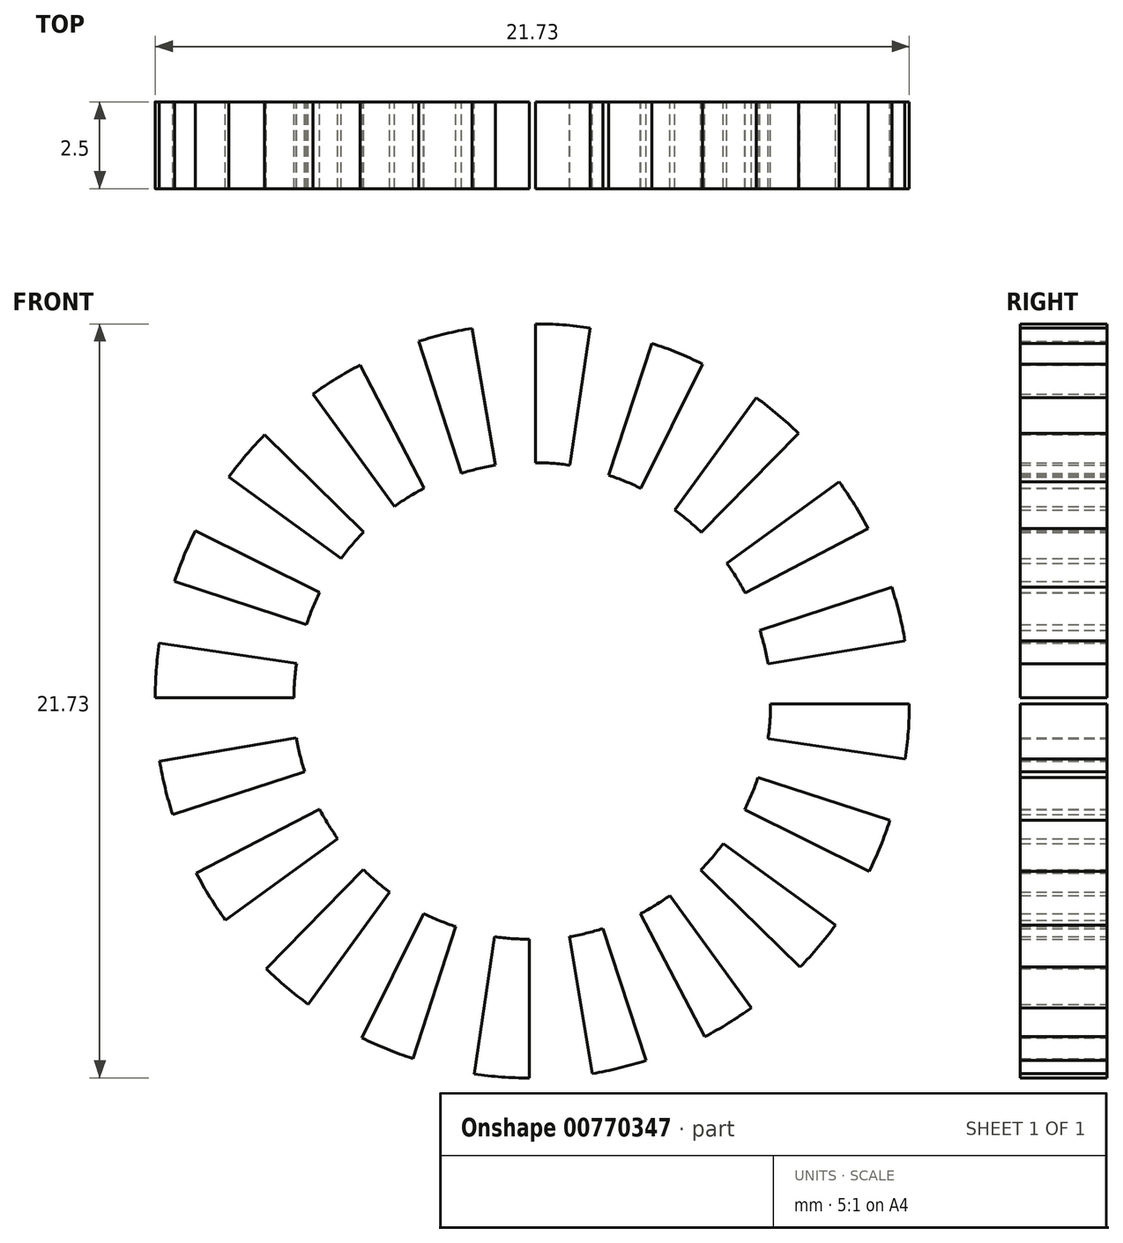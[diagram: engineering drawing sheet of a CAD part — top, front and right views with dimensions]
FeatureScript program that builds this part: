
annotation { "Feature Type Name" : "Feature", "Feature Type Description" : "" }
export const myFeature = defineFeature(function(context is Context, id is Id, definition is map)
    precondition{}
    {
        {
            var Q0;
            Q0=qCreatedBy(makeId("Front.planeOp"),FACE);
            var sketch = newSketch(context, id + "F0", { "sketchPlane" : qUnion([Q0])});
            skCircle(sketch, "E0", {"center": v(0, 0) * mm, "radius": 11.8 * mm});
            skSolve(sketch);
        }
        {
            var Q0;
            Q0=makeQuery(id+"F0.imprint","IMPRINT",FACE,{"disambiguationData":[TD([[makeQuery(id+"F0.imprint","IMPRINT",EDGE,{"derivedFrom":sQuery(id+"F0.wireOp",EDGE,"E0")}),1.0]])]});
            extrude(context, id + "F1", {"entities" : qUnion([Q0]), "endBound" : BoundingType.SYMMETRIC, "depth" : 2.5 * mm, "offsetDistance" : 25 * mm});
        }
        {
            var Q0;
            Q0=makeQuery(id+"F1.opExtrude","CAP_FACE",FACE,{"disambiguationData":[OSD([sQuery(id+"F0.wireOp",EDGE,"E0")])],"isStart":true});
            var sketch = newSketch(context, id + "F2", { "sketchPlane" : qUnion([Q0])});
            skArc(sketch, "E1", {"start": v(-1.58, 10.68) * mm, "mid": v(-0.8, 10.77) * mm, "end": v(0, 10.8) * mm});
            skArc(sketch, "E2", {"start": v(-1, 6.73) * mm, "mid": v(-0.5, 6.78) * mm, "end": v(0, 6.8) * mm});
            skLineSegment(sketch, "E3", {"start": v(-1, 6.73) * mm, "end": v(-1.58, 10.68) * mm});
            skLineSegment(sketch, "E4", {"start": v(0, 6.8) * mm, "end": v(0, 10.8) * mm});
            skArc(sketch, "E5.1.0", {"start": v(-4.82, 9.64) * mm, "mid": v(-4.1, 9.97) * mm, "end": v(-3.35, 10.24) * mm});
            skArc(sketch, "E5.1.1", {"start": v(-3.04, 6.06) * mm, "mid": v(-2.59, 6.26) * mm, "end": v(-2.12, 6.44) * mm});
            skLineSegment(sketch, "E5.1.2", {"start": v(-2.12, 6.44) * mm, "end": v(-3.35, 10.24) * mm});
            skLineSegment(sketch, "E5.1.3", {"start": v(-3.04, 6.06) * mm, "end": v(-4.82, 9.64) * mm});
            skArc(sketch, "E5.2.0", {"start": v(-7.58, 7.65) * mm, "mid": v(-7, 8.18) * mm, "end": v(-6.37, 8.67) * mm});
            skArc(sketch, "E5.2.1", {"start": v(-4.78, 4.8) * mm, "mid": v(-4.41, 5.13) * mm, "end": v(-4.02, 5.44) * mm});
            skLineSegment(sketch, "E5.2.2", {"start": v(-4.02, 5.44) * mm, "end": v(-6.37, 8.67) * mm});
            skLineSegment(sketch, "E5.2.3", {"start": v(-4.78, 4.8) * mm, "end": v(-7.58, 7.65) * mm});
            skArc(sketch, "E5.3.0", {"start": v(-9.6, 4.9) * mm, "mid": v(-9.2, 5.6) * mm, "end": v(-8.76, 6.25) * mm});
            skArc(sketch, "E5.3.1", {"start": v(-6.05, 3.05) * mm, "mid": v(-5.8, 3.48) * mm, "end": v(-5.52, 3.9) * mm});
            skLineSegment(sketch, "E5.3.2", {"start": v(-5.52, 3.9) * mm, "end": v(-8.76, 6.25) * mm});
            skLineSegment(sketch, "E5.3.3", {"start": v(-6.05, 3.05) * mm, "end": v(-9.6, 4.9) * mm});
            skArc(sketch, "E5.4.0", {"start": v(-10.65, 1.67) * mm, "mid": v(-10.5, 2.44) * mm, "end": v(-10.28, 3.2) * mm});
            skArc(sketch, "E5.4.1", {"start": v(-6.7, 1) * mm, "mid": v(-6.6, 1.5) * mm, "end": v(-6.47, 1.97) * mm});
            skLineSegment(sketch, "E5.4.2", {"start": v(-6.47, 1.97) * mm, "end": v(-10.28, 3.2) * mm});
            skLineSegment(sketch, "E5.4.3", {"start": v(-6.7, 1) * mm, "end": v(-10.65, 1.67) * mm});
            skArc(sketch, "E5.5.0", {"start": v(-10.66, -1.74) * mm, "mid": v(-10.75, -0.95) * mm, "end": v(-10.78, -0.15) * mm});
            skArc(sketch, "E5.5.1", {"start": v(-6.7, -1.15) * mm, "mid": v(-6.76, -0.65) * mm, "end": v(-6.78, -0.15) * mm});
            skLineSegment(sketch, "E5.5.2", {"start": v(-6.78, -0.15) * mm, "end": v(-10.78, -0.15) * mm});
            skLineSegment(sketch, "E5.5.3", {"start": v(-6.7, -1.15) * mm, "end": v(-10.66, -1.74) * mm});
            skArc(sketch, "E5.6.0", {"start": v(-9.62, -4.98) * mm, "mid": v(-9.95, -4.25) * mm, "end": v(-10.22, -3.5) * mm});
            skArc(sketch, "E5.6.1", {"start": v(-6.04, -3.2) * mm, "mid": v(-6.24, -2.74) * mm, "end": v(-6.42, -2.27) * mm});
            skLineSegment(sketch, "E5.6.2", {"start": v(-6.42, -2.27) * mm, "end": v(-10.22, -3.5) * mm});
            skLineSegment(sketch, "E5.6.3", {"start": v(-6.04, -3.2) * mm, "end": v(-9.62, -4.98) * mm});
            skArc(sketch, "E5.7.0", {"start": v(-7.63, -7.74) * mm, "mid": v(-8.16, -7.15) * mm, "end": v(-8.65, -6.53) * mm});
            skArc(sketch, "E5.7.1", {"start": v(-4.77, -4.94) * mm, "mid": v(-5.1, -4.57) * mm, "end": v(-5.42, -4.17) * mm});
            skLineSegment(sketch, "E5.7.2", {"start": v(-5.42, -4.17) * mm, "end": v(-8.65, -6.53) * mm});
            skLineSegment(sketch, "E5.7.3", {"start": v(-4.77, -4.94) * mm, "end": v(-7.63, -7.74) * mm});
            skArc(sketch, "E5.8.0", {"start": v(-4.88, -9.75) * mm, "mid": v(-5.57, -9.35) * mm, "end": v(-6.23, -8.91) * mm});
            skArc(sketch, "E5.8.1", {"start": v(-3.03, -6.2) * mm, "mid": v(-3.46, -5.95) * mm, "end": v(-3.88, -5.67) * mm});
            skLineSegment(sketch, "E5.8.2", {"start": v(-3.88, -5.67) * mm, "end": v(-6.23, -8.91) * mm});
            skLineSegment(sketch, "E5.8.3", {"start": v(-3.03, -6.2) * mm, "end": v(-4.88, -9.75) * mm});
            skArc(sketch, "E5.9.0", {"start": v(-1.65, -10.8) * mm, "mid": v(-2.42, -10.65) * mm, "end": v(-3.19, -10.43) * mm});
            skArc(sketch, "E5.9.1", {"start": v(-0.98, -6.86) * mm, "mid": v(-1.47, -6.76) * mm, "end": v(-1.95, -6.63) * mm});
            skLineSegment(sketch, "E5.9.2", {"start": v(-1.95, -6.63) * mm, "end": v(-3.19, -10.43) * mm});
            skLineSegment(sketch, "E5.9.3", {"start": v(-0.98, -6.86) * mm, "end": v(-1.65, -10.8) * mm});
            skArc(sketch, "E5.10.0", {"start": v(1.76, -10.82) * mm, "mid": v(0.97, -10.9) * mm, "end": v(0.17, -10.93) * mm});
            skArc(sketch, "E5.10.1", {"start": v(1.17, -6.86) * mm, "mid": v(0.67, -6.92) * mm, "end": v(0.17, -6.93) * mm});
            skLineSegment(sketch, "E5.10.2", {"start": v(0.17, -6.93) * mm, "end": v(0.17, -10.93) * mm});
            skLineSegment(sketch, "E5.10.3", {"start": v(1.17, -6.86) * mm, "end": v(1.76, -10.82) * mm});
            skArc(sketch, "E5.11.0", {"start": v(5, -9.78) * mm, "mid": v(4.27, -10.1) * mm, "end": v(3.53, -10.38) * mm});
            skArc(sketch, "E5.11.1", {"start": v(3.22, -6.2) * mm, "mid": v(2.76, -6.4) * mm, "end": v(2.3, -6.57) * mm});
            skLineSegment(sketch, "E5.11.2", {"start": v(2.3, -6.57) * mm, "end": v(3.53, -10.38) * mm});
            skLineSegment(sketch, "E5.11.3", {"start": v(3.22, -6.2) * mm, "end": v(5, -9.78) * mm});
            skArc(sketch, "E5.12.0", {"start": v(7.76, -7.78) * mm, "mid": v(7.17, -8.32) * mm, "end": v(6.55, -8.8) * mm});
            skArc(sketch, "E5.12.1", {"start": v(4.96, -4.93) * mm, "mid": v(4.59, -5.26) * mm, "end": v(4.2, -5.57) * mm});
            skLineSegment(sketch, "E5.12.2", {"start": v(4.2, -5.57) * mm, "end": v(6.55, -8.8) * mm});
            skLineSegment(sketch, "E5.12.3", {"start": v(4.96, -4.93) * mm, "end": v(7.76, -7.78) * mm});
            skArc(sketch, "E5.13.0", {"start": v(9.77, -5.03) * mm, "mid": v(9.37, -5.72) * mm, "end": v(8.93, -6.38) * mm});
            skArc(sketch, "E5.13.1", {"start": v(6.22, -3.18) * mm, "mid": v(5.97, -3.62) * mm, "end": v(5.7, -4.03) * mm});
            skLineSegment(sketch, "E5.13.2", {"start": v(5.7, -4.03) * mm, "end": v(8.93, -6.38) * mm});
            skLineSegment(sketch, "E5.13.3", {"start": v(6.22, -3.18) * mm, "end": v(9.77, -5.03) * mm});
            skArc(sketch, "E5.14.0", {"start": v(10.83, -1.8) * mm, "mid": v(10.67, -2.58) * mm, "end": v(10.45, -3.34) * mm});
            skArc(sketch, "E5.14.1", {"start": v(6.88, -1.14) * mm, "mid": v(6.78, -1.63) * mm, "end": v(6.65, -2.1) * mm});
            skLineSegment(sketch, "E5.14.2", {"start": v(6.65, -2.1) * mm, "end": v(10.45, -3.34) * mm});
            skLineSegment(sketch, "E5.14.3", {"start": v(6.88, -1.14) * mm, "end": v(10.83, -1.8) * mm});
            skArc(sketch, "E5.15.0", {"start": v(10.84, 1.6) * mm, "mid": v(10.93, 0.81) * mm, "end": v(10.95, 0.02) * mm});
            skArc(sketch, "E5.15.1", {"start": v(6.88, 1.02) * mm, "mid": v(6.94, 0.52) * mm, "end": v(6.95, 0.02) * mm});
            skLineSegment(sketch, "E5.15.2", {"start": v(6.95, 0.02) * mm, "end": v(10.95, 0.02) * mm});
            skLineSegment(sketch, "E5.15.3", {"start": v(6.88, 1.02) * mm, "end": v(10.84, 1.6) * mm});
            skArc(sketch, "E5.16.0", {"start": v(9.8, 4.84) * mm, "mid": v(10.12, 4.12) * mm, "end": v(10.4, 3.37) * mm});
            skArc(sketch, "E5.16.1", {"start": v(6.21, 3.06) * mm, "mid": v(6.42, 2.6) * mm, "end": v(6.6, 2.14) * mm});
            skLineSegment(sketch, "E5.16.2", {"start": v(6.6, 2.14) * mm, "end": v(10.4, 3.37) * mm});
            skLineSegment(sketch, "E5.16.3", {"start": v(6.21, 3.06) * mm, "end": v(9.8, 4.84) * mm});
            skArc(sketch, "E5.17.0", {"start": v(7.8, 7.6) * mm, "mid": v(8.34, 7.02) * mm, "end": v(8.83, 6.4) * mm});
            skArc(sketch, "E5.17.1", {"start": v(4.95, 4.8) * mm, "mid": v(5.28, 4.43) * mm, "end": v(5.6, 4.04) * mm});
            skLineSegment(sketch, "E5.17.2", {"start": v(5.6, 4.04) * mm, "end": v(8.83, 6.4) * mm});
            skLineSegment(sketch, "E5.17.3", {"start": v(4.95, 4.8) * mm, "end": v(7.8, 7.6) * mm});
            skArc(sketch, "E5.18.0", {"start": v(5.05, 9.61) * mm, "mid": v(5.74, 9.22) * mm, "end": v(6.4, 8.78) * mm});
            skArc(sketch, "E5.18.1", {"start": v(3.2, 6.07) * mm, "mid": v(3.64, 5.82) * mm, "end": v(4.05, 5.54) * mm});
            skLineSegment(sketch, "E5.18.2", {"start": v(4.05, 5.54) * mm, "end": v(6.4, 8.78) * mm});
            skLineSegment(sketch, "E5.18.3", {"start": v(3.2, 6.07) * mm, "end": v(5.05, 9.61) * mm});
            skArc(sketch, "E5.19.0", {"start": v(1.82, 10.67) * mm, "mid": v(2.6, 10.51) * mm, "end": v(3.36, 10.3) * mm});
            skArc(sketch, "E5.19.1", {"start": v(1.16, 6.73) * mm, "mid": v(1.65, 6.63) * mm, "end": v(2.13, 6.5) * mm});
            skLineSegment(sketch, "E5.19.2", {"start": v(2.13, 6.5) * mm, "end": v(3.36, 10.3) * mm});
            skLineSegment(sketch, "E5.19.3", {"start": v(1.16, 6.73) * mm, "end": v(1.82, 10.67) * mm});
            skPoint(sketch, "E5.center", {"position": v(0.09, -0.07) * mm});
            skSolve(sketch);
        }
        {
            var Q0;
            Q0=makeQuery(id+"F2.imprint","IMPRINT",FACE,{"disambiguationData":[TD([[makeQuery(id+"F2.imprint","IMPRINT",EDGE,{"derivedFrom":sQuery(id+"F2.wireOp",EDGE,"E1")}),-1.0]])]});
            var Q1;
            Q1=makeQuery(id+"F2.imprint","IMPRINT",FACE,{"disambiguationData":[TD([[makeQuery(id+"F2.imprint","IMPRINT",EDGE,{"derivedFrom":sQuery(id+"F2.wireOp",EDGE,"E5.2.0")}),-1.0]])]});
            var Q2;
            Q2=makeQuery(id+"F2.imprint","IMPRINT",FACE,{"disambiguationData":[TD([[makeQuery(id+"F2.imprint","IMPRINT",EDGE,{"derivedFrom":sQuery(id+"F2.wireOp",EDGE,"E5.3.0")}),-1.0]])]});
            var Q3;
            Q3=makeQuery(id+"F2.imprint","IMPRINT",FACE,{"disambiguationData":[TD([[makeQuery(id+"F2.imprint","IMPRINT",EDGE,{"derivedFrom":sQuery(id+"F2.wireOp",EDGE,"E5.4.0")}),-1.0]])]});
            var Q4;
            Q4=makeQuery(id+"F2.imprint","IMPRINT",FACE,{"disambiguationData":[TD([[makeQuery(id+"F2.imprint","IMPRINT",EDGE,{"derivedFrom":sQuery(id+"F2.wireOp",EDGE,"E5.5.0")}),-1.0]])]});
            var Q5;
            Q5=makeQuery(id+"F2.imprint","IMPRINT",FACE,{"disambiguationData":[TD([[makeQuery(id+"F2.imprint","IMPRINT",EDGE,{"derivedFrom":sQuery(id+"F2.wireOp",EDGE,"E5.6.0")}),-1.0]])]});
            var Q6;
            Q6=makeQuery(id+"F2.imprint","IMPRINT",FACE,{"disambiguationData":[TD([[makeQuery(id+"F2.imprint","IMPRINT",EDGE,{"derivedFrom":sQuery(id+"F2.wireOp",EDGE,"E5.7.0")}),-1.0]])]});
            var Q7;
            Q7=makeQuery(id+"F2.imprint","IMPRINT",FACE,{"disambiguationData":[TD([[makeQuery(id+"F2.imprint","IMPRINT",EDGE,{"derivedFrom":sQuery(id+"F2.wireOp",EDGE,"E5.8.0")}),-1.0]])]});
            var Q8;
            Q8=makeQuery(id+"F2.imprint","IMPRINT",FACE,{"disambiguationData":[TD([[makeQuery(id+"F2.imprint","IMPRINT",EDGE,{"derivedFrom":sQuery(id+"F2.wireOp",EDGE,"E5.9.0")}),-1.0]])]});
            var Q9;
            Q9=makeQuery(id+"F2.imprint","IMPRINT",FACE,{"disambiguationData":[TD([[makeQuery(id+"F2.imprint","IMPRINT",EDGE,{"derivedFrom":sQuery(id+"F2.wireOp",EDGE,"E5.10.0")}),-1.0]])]});
            var Q10;
            Q10=makeQuery(id+"F2.imprint","IMPRINT",FACE,{"disambiguationData":[TD([[makeQuery(id+"F2.imprint","IMPRINT",EDGE,{"derivedFrom":sQuery(id+"F2.wireOp",EDGE,"E5.11.0")}),-1.0]])]});
            var Q11;
            Q11=makeQuery(id+"F2.imprint","IMPRINT",FACE,{"disambiguationData":[TD([[makeQuery(id+"F2.imprint","IMPRINT",EDGE,{"derivedFrom":sQuery(id+"F2.wireOp",EDGE,"E5.12.0")}),-1.0]])]});
            var Q12;
            Q12=makeQuery(id+"F2.imprint","IMPRINT",FACE,{"disambiguationData":[TD([[makeQuery(id+"F2.imprint","IMPRINT",EDGE,{"derivedFrom":sQuery(id+"F2.wireOp",EDGE,"E5.13.0")}),-1.0]])]});
            var Q13;
            Q13=makeQuery(id+"F2.imprint","IMPRINT",FACE,{"disambiguationData":[TD([[makeQuery(id+"F2.imprint","IMPRINT",EDGE,{"derivedFrom":sQuery(id+"F2.wireOp",EDGE,"E5.14.0")}),-1.0]])]});
            var Q14;
            Q14=makeQuery(id+"F2.imprint","IMPRINT",FACE,{"disambiguationData":[TD([[makeQuery(id+"F2.imprint","IMPRINT",EDGE,{"derivedFrom":sQuery(id+"F2.wireOp",EDGE,"E5.15.0")}),-1.0]])]});
            var Q15;
            Q15=makeQuery(id+"F2.imprint","IMPRINT",FACE,{"disambiguationData":[TD([[makeQuery(id+"F2.imprint","IMPRINT",EDGE,{"derivedFrom":sQuery(id+"F2.wireOp",EDGE,"E5.16.0")}),-1.0]])]});
            var Q16;
            Q16=makeQuery(id+"F2.imprint","IMPRINT",FACE,{"disambiguationData":[TD([[makeQuery(id+"F2.imprint","IMPRINT",EDGE,{"derivedFrom":sQuery(id+"F2.wireOp",EDGE,"E5.17.0")}),-1.0]])]});
            var Q17;
            Q17=makeQuery(id+"F2.imprint","IMPRINT",FACE,{"disambiguationData":[TD([[makeQuery(id+"F2.imprint","IMPRINT",EDGE,{"derivedFrom":sQuery(id+"F2.wireOp",EDGE,"E5.18.0")}),-1.0]])]});
            var Q18;
            Q18=makeQuery(id+"F2.imprint","IMPRINT",FACE,{"disambiguationData":[TD([[makeQuery(id+"F2.imprint","IMPRINT",EDGE,{"derivedFrom":sQuery(id+"F2.wireOp",EDGE,"E5.19.0")}),-1.0]])]});
            var Q19;
            Q19=makeQuery(id+"F2.imprint","IMPRINT",FACE,{"disambiguationData":[TD([[makeQuery(id+"F2.imprint","IMPRINT",EDGE,{"derivedFrom":sQuery(id+"F2.wireOp",EDGE,"E5.1.0")}),-1.0]])]});
            extrude(context, id + "F3", {"entities" : qUnion([Q0, Q1, Q2, Q3, Q4, Q5, Q6, Q7, Q8, Q9, Q10, Q11, Q12, Q13, Q14, Q15, Q16, Q17, Q18, Q19]), "operationType" : NewBodyOperationType.REMOVE, "endBound" : BoundingType.THROUGH_ALL, "oppositeDirection" : true, "depth" : 25 * mm, "offsetDistance" : 25 * mm});
        }
        {
            var Q0;
            Q0=makeQuery(id+"F1.opExtrude","CAP_FACE",FACE,{"disambiguationData":[OSD([sQuery(id+"F0.wireOp",EDGE,"E0")])],"isStart":true});
            var sketch = newSketch(context, id + "F4", { "sketchPlane" : qUnion([Q0])});
            skLineSegment(sketch, "E6", {"start": v(-1.75, -2.12) * mm, "end": v(-1.75, 2.12) * mm});
            skLineSegment(sketch, "E7", {"start": v(1.75, -2.12) * mm, "end": v(1.75, 2.12) * mm});
            skArc(sketch, "E8", {"start": v(-1.75, 2.12) * mm, "mid": v(0, 2.75) * mm, "end": v(1.75, 2.12) * mm});
            skArc(sketch, "E9", {"start": v(1.75, -2.12) * mm, "mid": v(0, -2.75) * mm, "end": v(-1.75, -2.12) * mm});
            skSolve(sketch);
        }
        {
            var Q0;
            Q0 = qSketchRegion(id + "F4", true);
            extrude(context, id + "F5", {"entities" : qUnion([Q0]), "operationType" : NewBodyOperationType.REMOVE, "endBound" : BoundingType.THROUGH_ALL, "oppositeDirection" : true, "depth" : 25 * mm, "offsetDistance" : 25 * mm});
        }
    });
